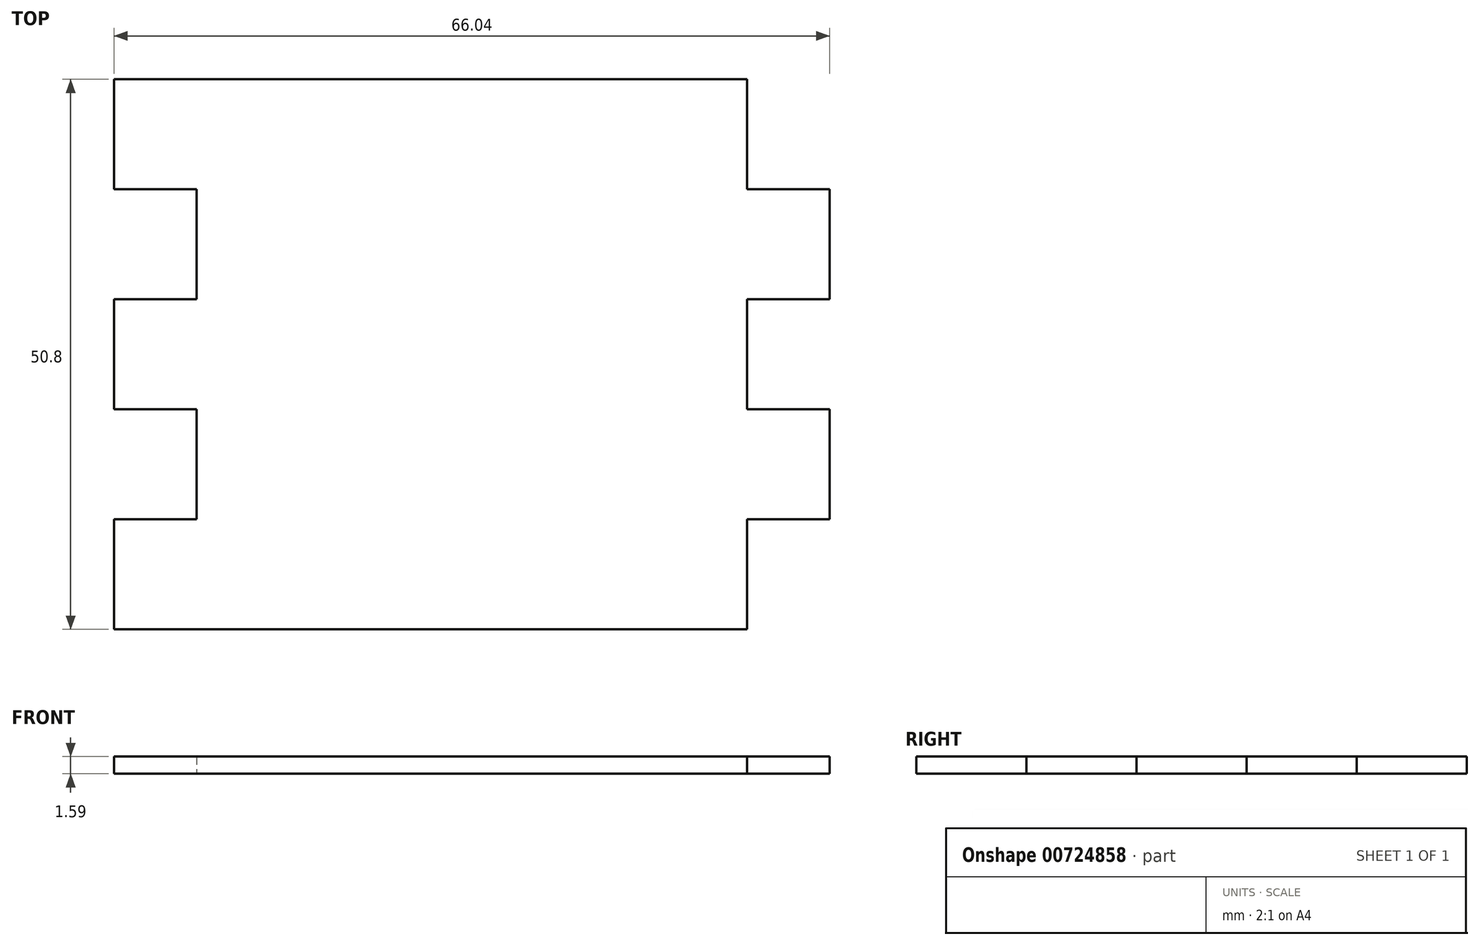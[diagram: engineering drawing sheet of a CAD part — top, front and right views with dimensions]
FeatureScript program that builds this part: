
annotation { "Feature Type Name" : "Feature", "Feature Type Description" : "" }
export const myFeature = defineFeature(function(context is Context, id is Id, definition is map)
    precondition{}
    {
        {
            var Q0;
            Q0=qCreatedBy(makeId("Top.planeOp"),FACE);
            var sketch = newSketch(context, id + "F0", { "sketchPlane" : qUnion([Q0])});
            skLineSegment(sketch, "E0.bottom", {"start": v(25.4, 25.4) * mm, "end": v(-25.4, 25.4) * mm});
            skLineSegment(sketch, "E0.top", {"start": v(25.4, -25.4) * mm, "end": v(-25.4, -25.4) * mm});
            skLineSegment(sketch, "E0.left", {"start": v(25.4, 25.4) * mm, "end": v(25.4, -25.4) * mm});
            skLineSegment(sketch, "E0.right", {"start": v(-25.4, 25.4) * mm, "end": v(-25.4, -25.4) * mm});
            skPoint(sketch, "E0.middle", {"position": v(0, 0) * mm});
            skLineSegment(sketch, "E1", {"start": v(25.4, -25.4) * mm, "end": v(25.4, -15.24) * mm});
            skLineSegment(sketch, "E2.bottom", {"start": v(25.4, -15.24) * mm, "end": v(33.02, -15.24) * mm});
            skLineSegment(sketch, "E2.top", {"start": v(25.4, -5.08) * mm, "end": v(33.02, -5.08) * mm});
            skLineSegment(sketch, "E2.left", {"start": v(25.4, -15.24) * mm, "end": v(25.4, -5.08) * mm});
            skLineSegment(sketch, "E2.right", {"start": v(33.02, -15.24) * mm, "end": v(33.02, -5.08) * mm});
            skLineSegment(sketch, "E3", {"start": v(25.4, -5.08) * mm, "end": v(25.4, 5.08) * mm});
            skLineSegment(sketch, "E4.bottom", {"start": v(25.4, 5.08) * mm, "end": v(33.02, 5.08) * mm});
            skLineSegment(sketch, "E4.top", {"start": v(25.4, 15.24) * mm, "end": v(33.02, 15.24) * mm});
            skLineSegment(sketch, "E4.left", {"start": v(25.4, 5.08) * mm, "end": v(25.4, 15.24) * mm});
            skLineSegment(sketch, "E4.right", {"start": v(33.02, 5.08) * mm, "end": v(33.02, 15.24) * mm});
            skLineSegment(sketch, "E5", {"start": v(25.4, -25.4) * mm, "end": v(15.24, -25.4) * mm});
            skLineSegment(sketch, "E6.bottom", {"start": v(15.24, -25.4) * mm, "end": v(5.08, -25.4) * mm});
            skLineSegment(sketch, "E6.top", {"start": v(15.24, -33.02) * mm, "end": v(5.08, -33.02) * mm});
            skLineSegment(sketch, "E6.left", {"start": v(15.24, -25.4) * mm, "end": v(15.24, -33.02) * mm});
            skLineSegment(sketch, "E6.right", {"start": v(5.08, -25.4) * mm, "end": v(5.08, -33.02) * mm});
            skLineSegment(sketch, "E7", {"start": v(5.08, -25.4) * mm, "end": v(-5.08, -25.4) * mm});
            skLineSegment(sketch, "E8.bottom", {"start": v(-5.08, -25.4) * mm, "end": v(-15.24, -25.4) * mm});
            skLineSegment(sketch, "E8.top", {"start": v(-5.08, -33.02) * mm, "end": v(-15.24, -33.02) * mm});
            skLineSegment(sketch, "E8.left", {"start": v(-5.08, -25.4) * mm, "end": v(-5.08, -33.02) * mm});
            skLineSegment(sketch, "E8.right", {"start": v(-15.24, -25.4) * mm, "end": v(-15.24, -33.02) * mm});
            skLineSegment(sketch, "E9.bottom", {"start": v(15.24, 25.4) * mm, "end": v(5.08, 25.4) * mm});
            skLineSegment(sketch, "E9.top", {"start": v(15.24, 33.02) * mm, "end": v(5.08, 33.02) * mm});
            skLineSegment(sketch, "E9.left", {"start": v(15.24, 25.4) * mm, "end": v(15.24, 33.02) * mm});
            skLineSegment(sketch, "E9.right", {"start": v(5.08, 25.4) * mm, "end": v(5.08, 33.02) * mm});
            skLineSegment(sketch, "E10", {"start": v(5.08, 25.4) * mm, "end": v(-5.08, 25.4) * mm});
            skLineSegment(sketch, "E11.bottom", {"start": v(-5.08, 25.4) * mm, "end": v(-15.24, 25.4) * mm});
            skLineSegment(sketch, "E11.top", {"start": v(-5.08, 33.02) * mm, "end": v(-15.24, 33.02) * mm});
            skLineSegment(sketch, "E11.left", {"start": v(-5.08, 25.4) * mm, "end": v(-5.08, 33.02) * mm});
            skLineSegment(sketch, "E11.right", {"start": v(-15.24, 25.4) * mm, "end": v(-15.24, 33.02) * mm});
            skLineSegment(sketch, "E12.bottom", {"start": v(-25.4, 25.4) * mm, "end": v(-33.02, 25.4) * mm});
            skLineSegment(sketch, "E12.top", {"start": v(-25.4, 15.24) * mm, "end": v(-33.02, 15.24) * mm});
            skLineSegment(sketch, "E12.left", {"start": v(-25.4, 25.4) * mm, "end": v(-25.4, 15.24) * mm});
            skLineSegment(sketch, "E12.right", {"start": v(-33.02, 25.4) * mm, "end": v(-33.02, 15.24) * mm});
            skLineSegment(sketch, "E13", {"start": v(-25.4, 15.24) * mm, "end": v(-25.4, 5.08) * mm});
            skLineSegment(sketch, "E14.bottom", {"start": v(-25.4, 5.08) * mm, "end": v(-33.02, 5.08) * mm});
            skLineSegment(sketch, "E14.top", {"start": v(-25.4, -5.08) * mm, "end": v(-33.02, -5.08) * mm});
            skLineSegment(sketch, "E14.left", {"start": v(-25.4, 5.08) * mm, "end": v(-25.4, -5.08) * mm});
            skLineSegment(sketch, "E14.right", {"start": v(-33.02, 5.08) * mm, "end": v(-33.02, -5.08) * mm});
            skLineSegment(sketch, "E15", {"start": v(-25.4, -5.08) * mm, "end": v(-25.4, -15.24) * mm});
            skLineSegment(sketch, "E16.bottom", {"start": v(-25.4, -15.24) * mm, "end": v(-33.02, -15.24) * mm});
            skLineSegment(sketch, "E16.top", {"start": v(-25.4, -25.4) * mm, "end": v(-33.02, -25.4) * mm});
            skLineSegment(sketch, "E16.left", {"start": v(-25.4, -15.24) * mm, "end": v(-25.4, -25.4) * mm});
            skLineSegment(sketch, "E16.right", {"start": v(-33.02, -15.24) * mm, "end": v(-33.02, -25.4) * mm});
            skSolve(sketch);
        }
        {
            var Q0;
            Q0=makeQuery(id+"F0.imprint","IMPRINT",FACE,{"disambiguationData":[TD([[makeQuery(id+"F0.imprint","IMPRINT",EDGE,{"derivedFrom":sQuery(id+"F0.wireOp",EDGE,"E0.top")}),-1.0]])]});
            var Q1;
            Q1=makeQuery(id+"F0.imprint","IMPRINT",FACE,{"disambiguationData":[TD([[makeQuery(id+"F0.imprint","IMPRINT",EDGE,{"derivedFrom":sQuery(id+"F0.wireOp",EDGE,"E14.bottom")}),1.0]])]});
            var Q2;
            Q2=makeQuery(id+"F0.imprint","IMPRINT",FACE,{"disambiguationData":[TD([[makeQuery(id+"F0.imprint","IMPRINT",EDGE,{"derivedFrom":sQuery(id+"F0.wireOp",EDGE,"E12.bottom")}),1.0]])]});
            var Q3;
            Q3=makeQuery(id+"F0.imprint","IMPRINT",FACE,{"disambiguationData":[TD([[makeQuery(id+"F0.imprint","IMPRINT",EDGE,{"derivedFrom":sQuery(id+"F0.wireOp",EDGE,"E11.bottom")}),-1.0]])]});
            var Q4;
            Q4=makeQuery(id+"F0.imprint","IMPRINT",FACE,{"disambiguationData":[TD([[makeQuery(id+"F0.imprint","IMPRINT",EDGE,{"derivedFrom":sQuery(id+"F0.wireOp",EDGE,"E9.bottom")}),-1.0]])]});
            var Q5;
            Q5=makeQuery(id+"F0.imprint","IMPRINT",FACE,{"disambiguationData":[TD([[makeQuery(id+"F0.imprint","IMPRINT",EDGE,{"derivedFrom":sQuery(id+"F0.wireOp",EDGE,"E4.bottom")}),1.0]])]});
            var Q6;
            Q6=makeQuery(id+"F0.imprint","IMPRINT",FACE,{"disambiguationData":[TD([[makeQuery(id+"F0.imprint","IMPRINT",EDGE,{"derivedFrom":sQuery(id+"F0.wireOp",EDGE,"E2.bottom")}),1.0]])]});
            var Q7;
            Q7=makeQuery(id+"F0.imprint","IMPRINT",FACE,{"disambiguationData":[TD([[makeQuery(id+"F0.imprint","IMPRINT",EDGE,{"derivedFrom":sQuery(id+"F0.wireOp",EDGE,"E6.bottom")}),1.0]])]});
            var Q8;
            Q8=makeQuery(id+"F0.imprint","IMPRINT",FACE,{"disambiguationData":[TD([[makeQuery(id+"F0.imprint","IMPRINT",EDGE,{"derivedFrom":sQuery(id+"F0.wireOp",EDGE,"E8.bottom")}),1.0]])]});
            var Q9;
            Q9=makeQuery(id+"F0.imprint","IMPRINT",FACE,{"disambiguationData":[TD([[makeQuery(id+"F0.imprint","IMPRINT",EDGE,{"derivedFrom":sQuery(id+"F0.wireOp",EDGE,"E16.bottom")}),1.0]])]});
            extrude(context, id + "F1", {"entities" : qUnion([Q0, Q1, Q2, Q3, Q4, Q5, Q6, Q7, Q8, Q9]), "depth" : 1.59 * mm, "offsetDistance" : 25.4 * mm});
        }
    });
